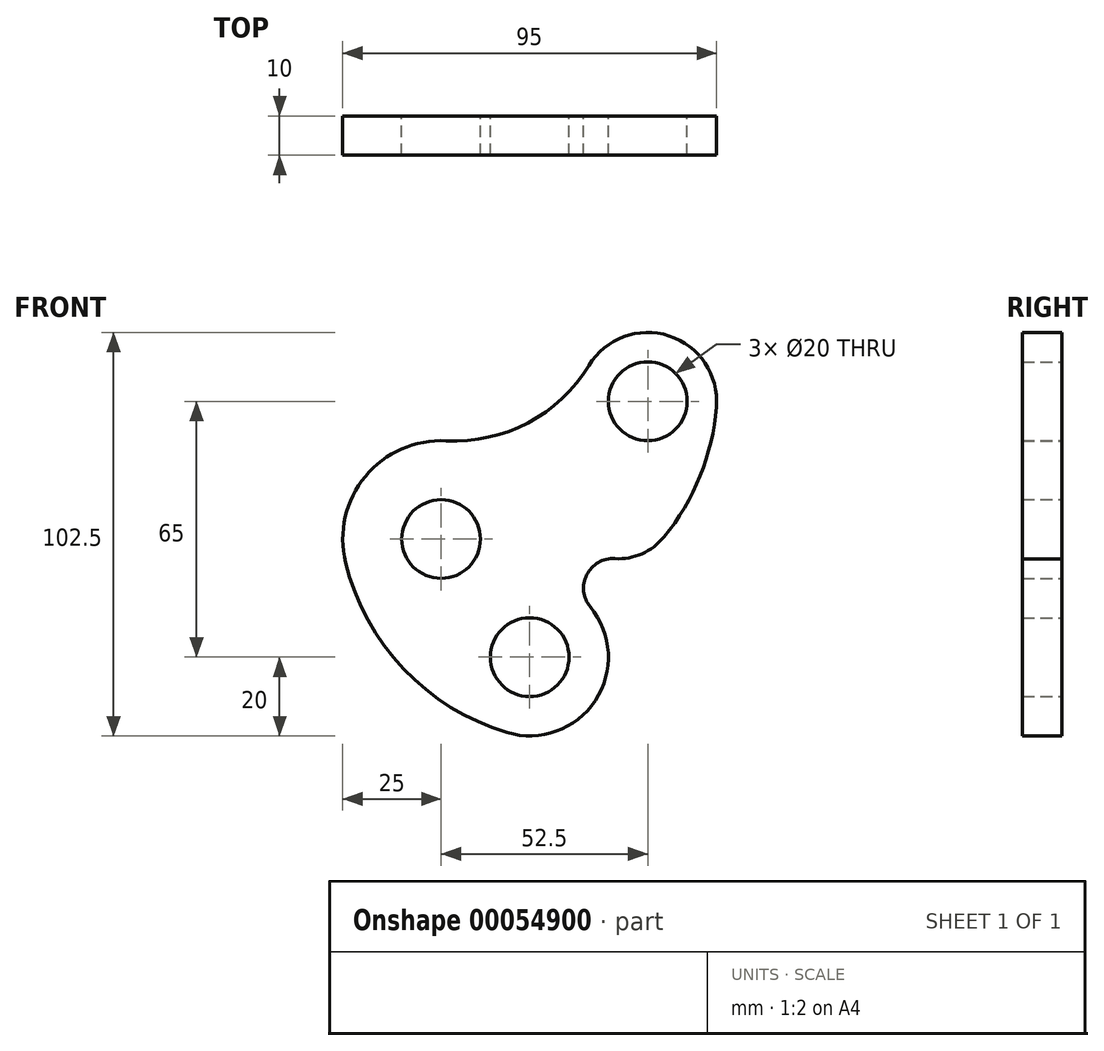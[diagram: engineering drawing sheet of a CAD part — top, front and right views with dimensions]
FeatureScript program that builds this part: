
annotation { "Feature Type Name" : "Feature", "Feature Type Description" : "" }
export const myFeature = defineFeature(function(context is Context, id is Id, definition is map)
    precondition{}
    {
        {
            var Q0;
            Q0=qCreatedBy(makeId("Front.planeOp"),FACE);
            var sketch = newSketch(context, id + "F0", { "sketchPlane" : qUnion([Q0])});
            skCircle(sketch, "E0", {"center": v(0, 0) * mm, "radius": 10 * mm});
            skCircle(sketch, "E1", {"center": v(52.5, 35) * mm, "radius": 10 * mm});
            skCircle(sketch, "E2", {"center": v(22.5, -30) * mm, "radius": 10 * mm});
            skArc(sketch, "E3", {"start": v(37.55, 44.1) * mm, "mid": v(57.9, 51.64) * mm, "end": v(69.94, 33.58) * mm});
            skArc(sketch, "E4", {"start": v(16.75, -49.16) * mm, "mid": v(39.17, -41.05) * mm, "end": v(37.9, -17.24) * mm});
            skArc(sketch, "E5", {"start": v(-24.28, -5.94) * mm, "mid": v(-19.26, 15.94) * mm, "end": v(1.3, 24.97) * mm});
            skArc(sketch, "E6", {"start": v(1.3, 24.97) * mm, "mid": v(22.07, 29.54) * mm, "end": v(37.55, 44.1) * mm});
            skArc(sketch, "E7", {"start": v(-24.28, -5.94) * mm, "mid": v(-9.51, -33) * mm, "end": v(16.75, -49.16) * mm});
            skArc(sketch, "E8", {"start": v(44.12, -4.97) * mm, "mid": v(51.03, -3.73) * mm, "end": v(56.62, 0.51) * mm});
            skArc(sketch, "E9", {"start": v(56.62, 0.51) * mm, "mid": v(65.8, 16.03) * mm, "end": v(69.94, 33.58) * mm});
            skArc(sketch, "E10", {"start": v(44.12, -4.97) * mm, "mid": v(37, -9.07) * mm, "end": v(37.9, -17.24) * mm});
            skSolve(sketch);
        }
        {
            var Q0;
            Q0=makeQuery(id+"F0.imprint","IMPRINT",FACE,{"disambiguationData":[TD([[makeQuery(id+"F0.imprint","IMPRINT",EDGE,{"derivedFrom":sQuery(id+"F0.wireOp",EDGE,"E0")}),-1.0]])]});
            extrude(context, id + "F1", {"entities" : qUnion([Q0]), "depth" : 10 * mm});
        }
    });
